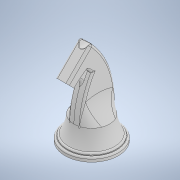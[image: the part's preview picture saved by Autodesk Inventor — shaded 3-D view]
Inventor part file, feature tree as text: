
AUTODESK INVENTOR PART (.ipt)
format: ipt  version: 2022 (Build 260153000, 153)  size: 600,064 bytes
history: native  units: mm
features: sketch x7, projected_geometry x5, fillet x4, other x3, extrude x3, sweep x2, revolve x1
ambient origin geometry x8: Origin, YZ Plane, XZ Plane, XY Plane, X Axis, Y Axis, Z Axis, Center Point
bodies: Solid1 (feature_tree)
feature tree (25):
  other  "Back Line Base.ipt"
  sketch  "Sketch1"  dims[d0=10.0mm d1=40.0mm]
  revolve  "Revolution1"  [1 undecoded]
  extrude  "Extrusion1"  Depth=20.0mm
  sweep  "Sweep1"
  sweep  "Sweep2"
  fillet  "Fillet5"  Radius=40.0mm
  fillet  "Fillet2"  [1 undecoded]
  extrude  "Extrusion5"  Depth=1.0mm TaperAngle=0.0deg
  fillet  "Fillet6"  [1 undecoded]
  extrude  "Extrusion6"  TaperAngle=0.0deg  [1 undecoded]
  fillet  "Fillet7"  Radius=12.0mm
  other  "Solid1::Back Line Base.ipt"
  other  "TaggingFeature1"
  projected_geometry  "Projected Loop1"
  sketch  "Sketch2"  dims[d8=17.0mm d10=20.0mm]
  projected_geometry  "Projected Loop2"
  projected_geometry  "Projected Loop3"
  sketch  "3D Sketch1"
  sketch  "Sketch3"  dims[d11=5.0mm d12=3.0mm]
  projected_geometry  "Projected Loop4"
  projected_geometry  "Projected Loop5"
  sketch  "3D Sketch2"
  sketch  "Sketch8"  dims[d14=3.0mm d16=35.0mm d17=40.0mm d18=90.0deg]
  sketch  "Sketch9"  dims[d19=16.0mm d20=6.0mm d21=0.0mm d22=0.0mm d23=0.0mm d24=0.0mm d25=0.0mm d27=12.0mm d28=45.0deg d29=7.0mm d43=1.0mm d44=4.0mm d45=7.0mm d46=0.0mm d47=0.3mm d48=2.0mm d49=0.0mm d50=1.0mm d51=8.0mm]
note: 4 required parameter values undecoded (feature->parameter linkage not recoverable at this tier; creation-order binding heuristic only, values carry confidence <= 0.55)